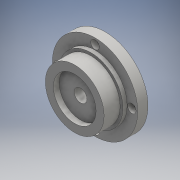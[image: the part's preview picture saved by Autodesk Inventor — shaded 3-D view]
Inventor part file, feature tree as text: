
AUTODESK INVENTOR PART (.ipt)
format: ipt  version: 2016 (Build 200138000, 138)  size: 168,448 bytes
history: native  units: mm
features: extrude x6, sketch x6, hole x4, other x1
ambient origin geometry x8: Origin, YZ Plane, XZ Plane, XY Plane, X Axis, Y Axis, Z Axis, Center Point
bodies: Body1 (feature_tree)
feature tree (17):
  other  "ソリッド1"
  extrude  "押し出し1"  Depth=80.0mm
  extrude  "押し出し2"  Depth=28.6mm TaperAngle=0.0deg
  extrude  "押し出し3"  Depth=60.1mm
  extrude  "押し出し4"  Depth=80.0mm
  extrude  "押し出し5"  Depth=19.0mm TaperAngle=0.0deg
  extrude  "押し出し6"  Depth=55.0mm
  hole  "穴1"  [1 undecoded]
  hole  "穴2"  [1 undecoded]
  hole  "穴3"  [1 undecoded]
  hole  "穴4"  [1 undecoded]
  sketch  "スケッチ1"
  sketch  "スケッチ2"
  sketch  "スケッチ3"
  sketch  "スケッチ5"
  sketch  "スケッチ6"
  sketch  "スケッチ7"
note: 4 required parameter values undecoded (feature->parameter linkage not recoverable at this tier; creation-order binding heuristic only, values carry confidence <= 0.55)
